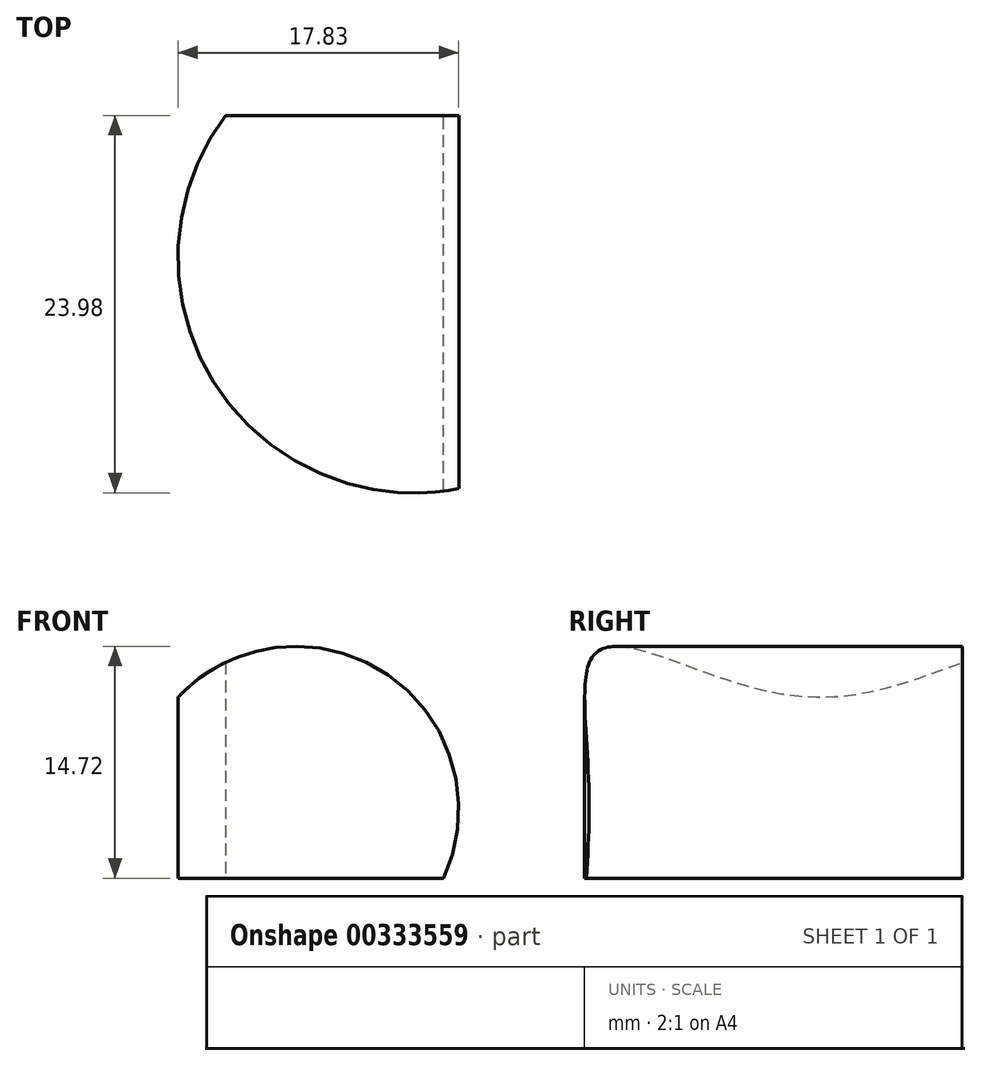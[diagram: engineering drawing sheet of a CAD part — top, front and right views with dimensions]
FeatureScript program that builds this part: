
annotation { "Feature Type Name" : "Feature", "Feature Type Description" : "" }
export const myFeature = defineFeature(function(context is Context, id is Id, definition is map)
    precondition{}
    {
        {
            var Q0;
            Q0=qCreatedBy(makeId("Right.planeOp"),FACE);
            var sketch = newSketch(context, id + "F0", { "sketchPlane" : qUnion([Q0])});
            skLineSegment(sketch, "E0", {"start": v(-53.34, 29.27) * mm, "end": v(5.52, 29.27) * mm});
            skLineSegment(sketch, "E1", {"start": v(5.52, 29.27) * mm, "end": v(5.52, -8.66) * mm});
            skLineSegment(sketch, "E2", {"start": v(5.52, -8.66) * mm, "end": v(-18.5, -8.66) * mm});
            skLineSegment(sketch, "E3", {"start": v(-18.5, -8.66) * mm, "end": v(-18.5, 12.92) * mm});
            skLineSegment(sketch, "E4", {"start": v(-18.5, 12.92) * mm, "end": v(-53.34, 12.92) * mm});
            skLineSegment(sketch, "E5", {"start": v(-53.34, 12.92) * mm, "end": v(-53.34, 29.27) * mm});
            skLineSegment(sketch, "E6", {"start": v(5.52, 29.27) * mm, "end": v(26.45, 29.27) * mm});
            skLineSegment(sketch, "E7", {"start": v(26.45, 29.27) * mm, "end": v(26.45, -8.66) * mm});
            skLineSegment(sketch, "E8", {"start": v(26.45, -8.66) * mm, "end": v(5.52, -8.66) * mm});
            skSolve(sketch);
        }
        {
            var Q0;
            Q0=makeQuery(id+"F0.imprint","IMPRINT",FACE,{"disambiguationData":[TD([[makeQuery(id+"F0.imprint","IMPRINT",EDGE,{"derivedFrom":sQuery(id+"F0.wireOp",EDGE,"E0")}),-1.0]])]});
            extrude(context, id + "F1", {"entities" : qUnion([Q0]), "depth" : 11.68 * mm});
        }
        {
            var Q0;
            Q0=makeQuery(id+"F0.imprint","IMPRINT",FACE,{"disambiguationData":[TD([[makeQuery(id+"F0.imprint","IMPRINT",EDGE,{"derivedFrom":sQuery(id+"F0.wireOp",EDGE,"E1")}),1.0]])]});
            extrude(context, id + "F2", {"entities" : qUnion([Q0]), "operationType" : NewBodyOperationType.ADD, "depth" : 31.5 * mm});
        }
        {
            var Q0;
            Q0=qCreatedBy(makeId("Top.planeOp"),FACE);
            var sketch = newSketch(context, id + "F3", { "sketchPlane" : qUnion([Q0])});
            skCircle(sketch, "E9", {"center": v(70.04, -9.01) * mm, "radius": 14.97 * mm});
            skSolve(sketch);
        }
        {
            var Q0;
            Q0=makeQuery(id+"F3.imprint","IMPRINT",FACE,{"disambiguationData":[TD([[makeQuery(id+"F3.imprint","IMPRINT",EDGE,{"derivedFrom":sQuery(id+"F3.wireOp",EDGE,"E9")}),1.0]])]});
            extrude(context, id + "F4", {"entities" : qUnion([Q0]), "depth" : 25.4 * mm});
        }
        {
            var Q0;
            Q0=qCreatedBy(makeId("Front.planeOp"),FACE);
            var sketch = newSketch(context, id + "F5", { "sketchPlane" : qUnion([Q0])});
            skCircle(sketch, "E10", {"center": v(82.93, 39.26) * mm, "radius": 6.32 * mm});
            skCircle(sketch, "E11", {"center": v(62.57, 4.39) * mm, "radius": 10.33 * mm});
            skSolve(sketch);
        }
        {
            var Q0;
            Q0 = qSketchRegion(id + "F5", true);
            extrude(context, id + "F6", {"entities" : qUnion([Q0]), "operationType" : NewBodyOperationType.INTERSECT, "depth" : 25.4 * mm});
        }
    });
